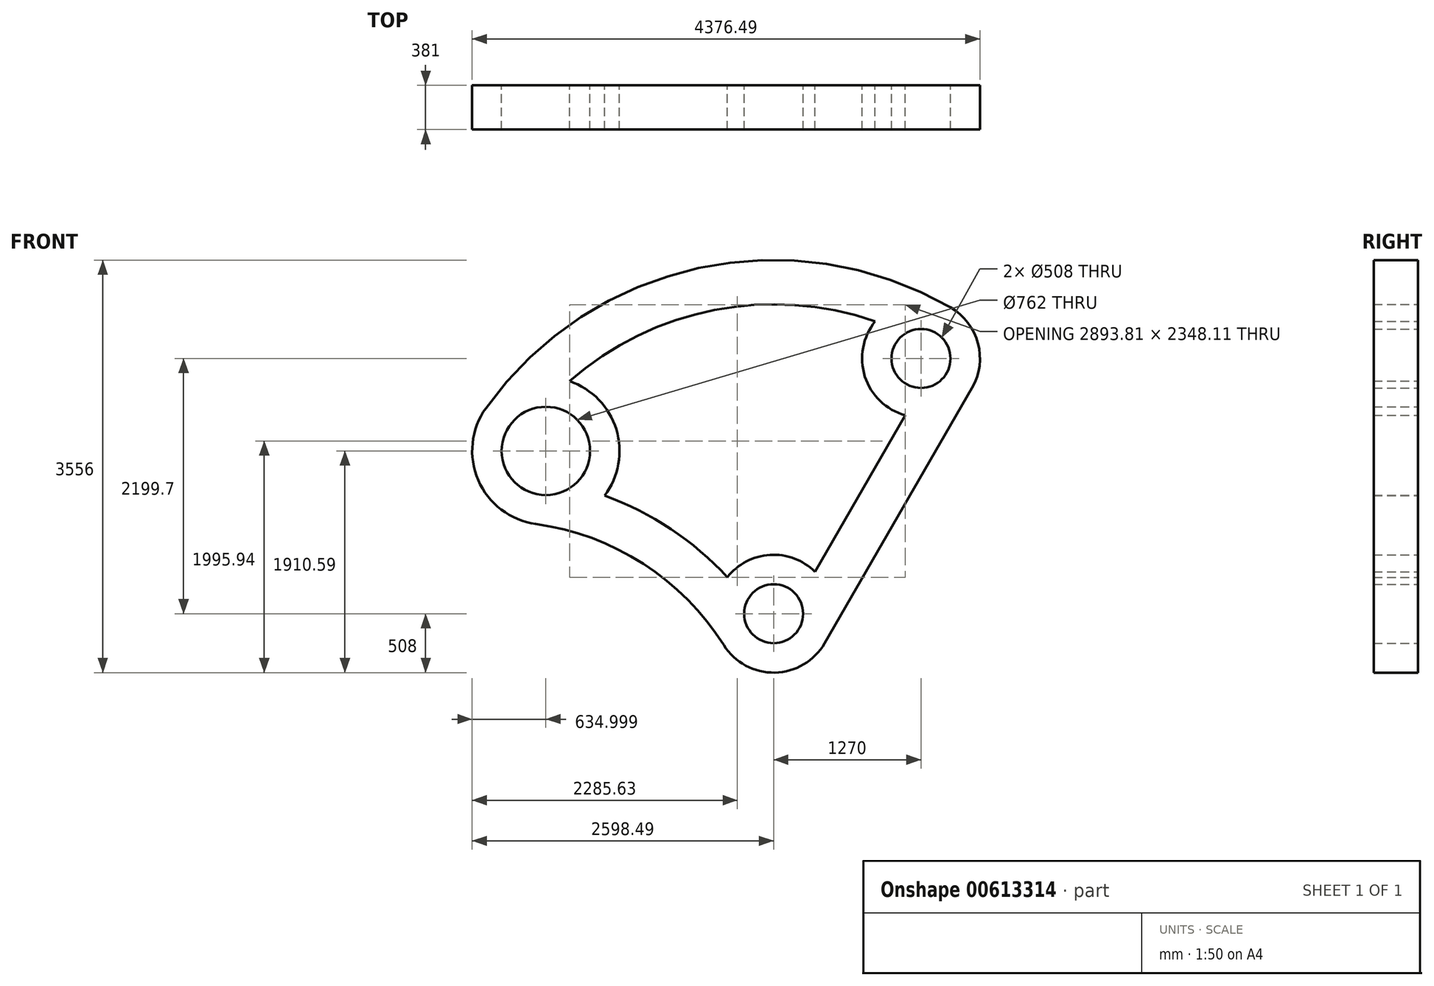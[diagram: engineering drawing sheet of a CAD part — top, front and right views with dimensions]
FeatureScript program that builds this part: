
annotation { "Feature Type Name" : "Feature", "Feature Type Description" : "" }
export const myFeature = defineFeature(function(context is Context, id is Id, definition is map)
    precondition{}
    {
        {
            var Q0;
            Q0=qCreatedBy(makeId("Front.planeOp"),FACE);
            var sketch = newSketch(context, id + "F0", { "sketchPlane" : qUnion([Q0])});
            skCircle(sketch, "E0", {"center": v(0, 0) * mm, "radius": 254 * mm});
            skArc(sketch, "E1", {"start": v(355.92, 362.47) * mm, "mid": v(-32.6, 506.95) * mm, "end": v(-399.42, 313.9) * mm});
            skArc(sketch, "E2", {"start": v(1524, 2639.65) * mm, "mid": v(-645.69, 2978.82) * mm, "end": v(-2480.2, 1771.7) * mm});
            skArc(sketch, "E3", {"start": v(875.15, 2519.33) * mm, "mid": v(-511.88, 2617.42) * mm, "end": v(-1759.76, 2004.03) * mm});
            skCircle(sketch, "E4", {"center": v(1270, 2199.7) * mm, "radius": 254 * mm});
            skArc(sketch, "E5", {"start": v(1709.94, 1945.7) * mm, "mid": v(1760.7, 2331.18) * mm, "end": v(1524, 2639.65) * mm});
            skLineSegment(sketch, "E6", {"start": v(439.94, -254) * mm, "end": v(1709.94, 1945.7) * mm});
            skLineSegment(sketch, "E7.0", {"start": v(355.92, 362.47) * mm, "end": v(1134.05, 1710.23) * mm});
            skCircle(sketch, "E8", {"center": v(-1963.5, 1402.6) * mm, "radius": 381 * mm});
            skArc(sketch, "E9", {"start": v(-1458.27, 1017.91) * mm, "mid": v(-1356.24, 1588.25) * mm, "end": v(-1759.76, 2004.03) * mm});
            skArc(sketch, "E10.trimOffspring", {"start": v(-429.62, -271.08) * mm, "mid": v(-1124.44, 430.48) * mm, "end": v(-2050.33, 773.56) * mm});
            skArc(sketch, "E11.0", {"start": v(-399.42, 313.9) * mm, "mid": v(-886.28, 729.93) * mm, "end": v(-1458.27, 1017.91) * mm});
            skArc(sketch, "E12.trimOffspring", {"start": v(-429.62, -271.08) * mm, "mid": v(9.98, -507.9) * mm, "end": v(439.94, -254) * mm});
            skArc(sketch, "E13.trimOffspring", {"start": v(-2480.2, 1771.7) * mm, "mid": v(-2546.7, 1151.42) * mm, "end": v(-2050.33, 773.56) * mm});
            skArc(sketch, "E14.trimOffspring", {"start": v(875.15, 2519.33) * mm, "mid": v(786.17, 2044.88) * mm, "end": v(1134.05, 1710.23) * mm});
            skSolve(sketch);
        }
        {
            var Q0;
            Q0=makeQuery(id+"F0.imprint","IMPRINT",FACE,{"disambiguationData":[TD([[makeQuery(id+"F0.imprint","IMPRINT",EDGE,{"derivedFrom":sQuery(id+"F0.wireOp",EDGE,"E0")}),-1.0]])]});
            extrude(context, id + "F1", {"entities" : qUnion([Q0]), "depth" : 381 * mm, "offsetDistance" : 25.4 * mm});
        }
    });
